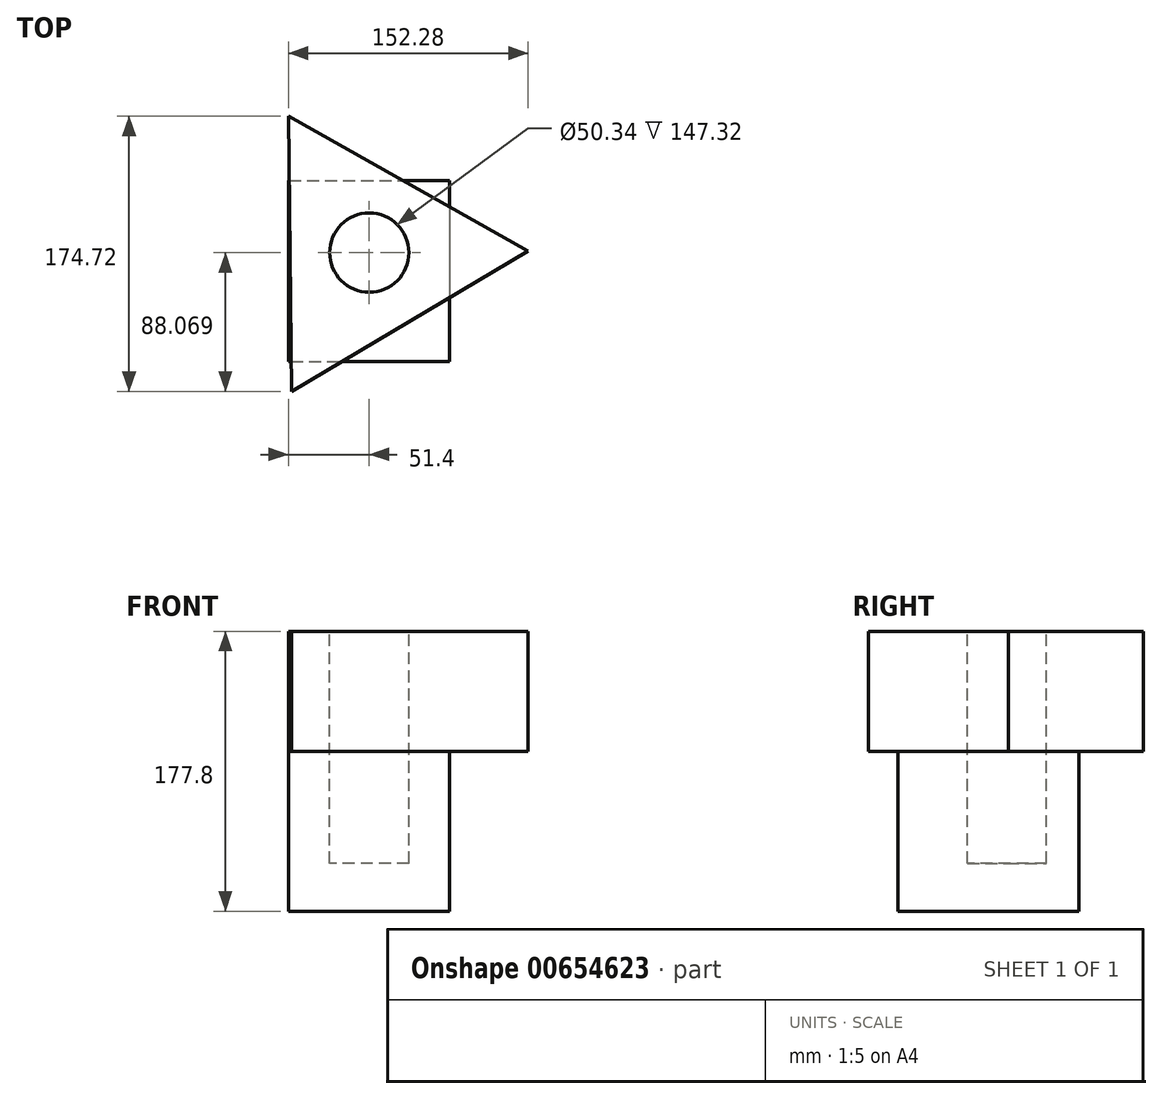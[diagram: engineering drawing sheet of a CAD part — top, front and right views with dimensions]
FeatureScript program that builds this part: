
annotation { "Feature Type Name" : "Feature", "Feature Type Description" : "" }
export const myFeature = defineFeature(function(context is Context, id is Id, definition is map)
    precondition{}
    {
        {
            var Q0;
            Q0=qCreatedBy(makeId("Top.planeOp"),FACE);
            var sketch = newSketch(context, id + "F0", { "sketchPlane" : qUnion([Q0])});
            skLineSegment(sketch, "E0.bottom", {"start": v(-51.11, 57.38) * mm, "end": v(51.11, 57.38) * mm});
            skLineSegment(sketch, "E0.top", {"start": v(-51.11, -57.38) * mm, "end": v(51.11, -57.38) * mm});
            skLineSegment(sketch, "E0.left", {"start": v(-51.11, 57.38) * mm, "end": v(-51.11, -57.38) * mm});
            skLineSegment(sketch, "E0.right", {"start": v(51.11, 57.38) * mm, "end": v(51.11, -57.38) * mm});
            skPoint(sketch, "E0.middle", {"position": v(0, 0) * mm});
            skSolve(sketch);
        }
        {
            var Q0;
            Q0 = qSketchRegion(id + "F0", true);
            extrude(context, id + "F1", {"entities" : qUnion([Q0]), "depth" : 101.6 * mm, "offsetDistance" : 25.4 * mm});
        }
        {
            var Q0;
            Q0=makeQuery(id+"F1.opExtrude","CAP_FACE",FACE,{"disambiguationData":[OSD([sQuery(id+"F0.wireOp",EDGE,"E0.bottom"),sQuery(id+"F0.wireOp",EDGE,"E0.top"),sQuery(id+"F0.wireOp",EDGE,"E0.left"),sQuery(id+"F0.wireOp",EDGE,"E0.right")])],"isStart":false});
            var sketch = newSketch(context, id + "F2", { "sketchPlane" : qUnion([Q0])});
            skCircle(sketch, "E1.cCircle", {"center": v(0, 11.6) * mm, "radius": 50.44 * mm, "construction": true});
            skLineSegment(sketch, "E1.0", {"start": v(100.88, 12.72) * mm, "end": v(-49.48, -76.3) * mm});
            skLineSegment(sketch, "E1.1", {"start": v(-49.48, -76.3) * mm, "end": v(-51.4, 98.41) * mm});
            skLineSegment(sketch, "E1.2", {"start": v(-51.4, 98.41) * mm, "end": v(100.88, 12.72) * mm});
            skPoint(sketch, "E1.0.midPoint", {"position": v(25.7, -31.8) * mm});
            skSolve(sketch);
        }
        {
            var Q0;
            Q0 = qSketchRegion(id + "F2", true);
            extrude(context, id + "F3", {"entities" : qUnion([Q0]), "operationType" : NewBodyOperationType.ADD, "depth" : 76.2 * mm, "offsetDistance" : 25.4 * mm});
        }
        {
            var Q0;
            Q0=makeQuery(id+"F3.opExtrude","CAP_FACE",FACE,{"disambiguationData":[OSD([sQuery(id+"F2.wireOp",EDGE,"E1.0"),sQuery(id+"F2.wireOp",EDGE,"E1.1"),sQuery(id+"F2.wireOp",EDGE,"E1.2")])],"isStart":false});
            var sketch = newSketch(context, id + "F4", { "sketchPlane" : qUnion([Q0])});
            skCircle(sketch, "E2", {"center": v(0, 11.76) * mm, "radius": 25.17 * mm});
            skSolve(sketch);
        }
        {
            var Q0;
            Q0 = qSketchRegion(id + "F4", true);
            extrude(context, id + "F5", {"entities" : qUnion([Q0]), "operationType" : NewBodyOperationType.REMOVE, "oppositeDirection" : true, "depth" : 147.32 * mm, "offsetDistance" : 25.4 * mm});
        }
    });
